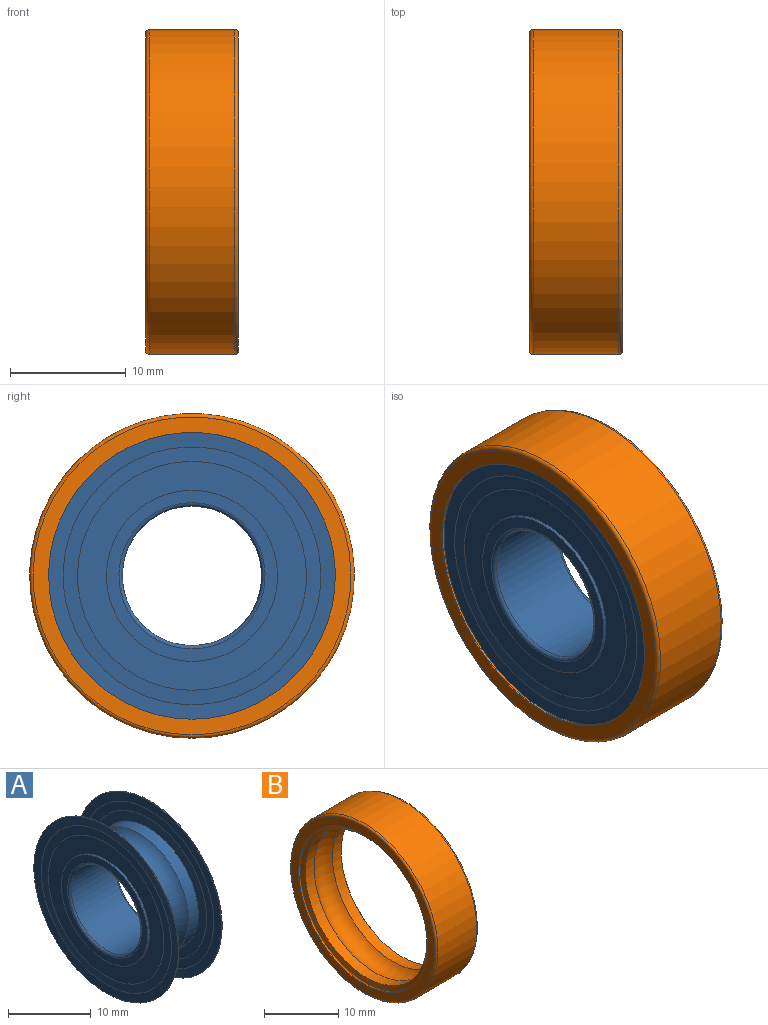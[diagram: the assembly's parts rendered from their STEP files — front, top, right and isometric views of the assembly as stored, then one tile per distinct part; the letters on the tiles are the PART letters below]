
ASSEMBLY  parts=2 mates=1
PART A: 28 faces, bbox 8x24.7x24.7 mm
  f0: cone r=12.36mm half-angle=85.9deg, axis (1,0,0), area 92.1mm2, adj f1,f27
  f1: plane 22.23x22.23mm, normal (-1,0,0), area 82.1mm2, adj f0,f2
  f2: cone r=9.87mm half-angle=87.9deg, axis (-1,0,0), area 134.5mm2, adj f1,f15
  f3: plane 14.75x14.75mm, normal (-1,0,0), area 46.2mm2, adj f5,f12
  f4: plane 14.75x14.75mm, normal (1,0,0), area 46.2mm2, adj f7,f13
  f5: cylinder r=7.38mm len=14.75mm, axis (-1,0,0), area 12.5mm2, adj f3,f20
  f6: torus R=7.6mm, axis (1,0,0), area 13mm2, adj f16,f21
  f7: torus R=6.3mm, axis (1,0,0), area 18.1mm2, adj f4,f11
  f8: cylinder r=8.5mm len=17mm, axis (-1,0,0), area 87.6mm2, adj f9,f16
  f9: torus R=10mm, axis (1,0,0), area 210.7mm2, adj f8,f10
  f10: cylinder r=8.5mm len=17mm, axis (-1,0,0), area 87.6mm2, adj f9,f14
  f11: cylinder r=6mm len=12mm, axis (-1,0,0), area 279mm2, adj f7,f12
  f12: torus R=6.3mm, axis (1,0,0), area 18.1mm2, adj f3,f11
  f13: cylinder r=7.38mm len=14.75mm, axis (-1,0,0), area 12.5mm2, adj f4,f24
  f14: plane 17x17mm, normal (1,0,0), area 45.5mm2, adj f10,f15
  f15: torus R=7.6mm, axis (1,0,0), area 13mm2, adj f2,f14
  f16: plane 17x17mm, normal (-1,0,0), area 45.5mm2, adj f6,f8
  f17: cylinder r=12.36mm len=24.72mm, axis (-1,0,0), area 7mm2, adj f18,f23
  f18: cone r=12.36mm half-angle=87.9deg, axis (-1,0,0), area 92mm2, adj f17,f19
  f19: cone r=11.11mm half-angle=87.9deg, axis (1,0,0), area 82.2mm2, adj f18,f20
  f20: plane 19.74x19.74mm, normal (-1,0,0), area 135mm2, adj f5,f19
  f21: cone r=7.38mm half-angle=87.9deg, axis (1,0,0), area 134.5mm2, adj f6,f22
  f22: plane 22.23x22.23mm, normal (1,0,0), area 82.1mm2, adj f21,f23
  f23: cone r=11.11mm half-angle=85.9deg, axis (-1,0,0), area 92.1mm2, adj f17,f22
  f24: plane 19.74x19.74mm, normal (1,0,0), area 135mm2, adj f13,f25
  f25: cone r=9.87mm half-angle=87.9deg, axis (-1,0,0), area 82.2mm2, adj f24,f26
  f26: cone r=11.11mm half-angle=87.9deg, axis (1,0,0), area 92mm2, adj f25,f27
  f27: cylinder r=12.36mm len=24.72mm, axis (-1,0,0), area 7mm2, adj f0,f26
PART B: 14 faces, bbox 8x30.3x30.3 mm
  f0: plane 27.4x27.4mm, normal (-1,0,0), area 109.7mm2, adj f1,f13
  f1: cylinder r=12.36mm len=24.72mm, axis (-1,0,0), area 7mm2, adj f0,f2
  f2: torus R=12.36mm, axis (1,0,0), area 44.3mm2, adj f1,f3
  f3: cone r=12.36mm half-angle=80deg, axis (-1,0,0), area 58.1mm2, adj f2,f4
  f4: cylinder r=11.6mm len=23.2mm, axis (-1,0,0), area 120.5mm2, adj f3,f5
  f5: torus R=10mm, axis (1,0,0), area 302.3mm2, adj f4,f6
  f6: cylinder r=11.6mm len=23.2mm, axis (-1,0,0), area 120.5mm2, adj f5,f7
  f7: cone r=11.6mm half-angle=80deg, axis (1,0,0), area 58.1mm2, adj f6,f8
  f8: torus R=12.36mm, axis (1,0,0), area 44.3mm2, adj f7,f9
  f9: cylinder r=12.36mm len=24.72mm, axis (-1,0,0), area 7mm2, adj f8,f10
  f10: plane 27.4x27.4mm, normal (1,0,0), area 109.7mm2, adj f9,f11
  f11: torus R=13.7mm, axis (1,0,0), area 41.1mm2, adj f10,f12
  f12: cylinder r=14mm len=28mm, axis (-1,0,0), area 650.9mm2, adj f11,f13
  f13: torus R=13.7mm, axis (1,0,0), area 41.1mm2, adj f0,f12
PLACE A t=(-8.54,-3.46,2.2)mm
PLACE B t=(-8.54,-3.46,2.2)mm
MATE fastened A.f0 <-> B.f1  axis (-1,0,0) through (-4.54,-3.46,2.2)mm
